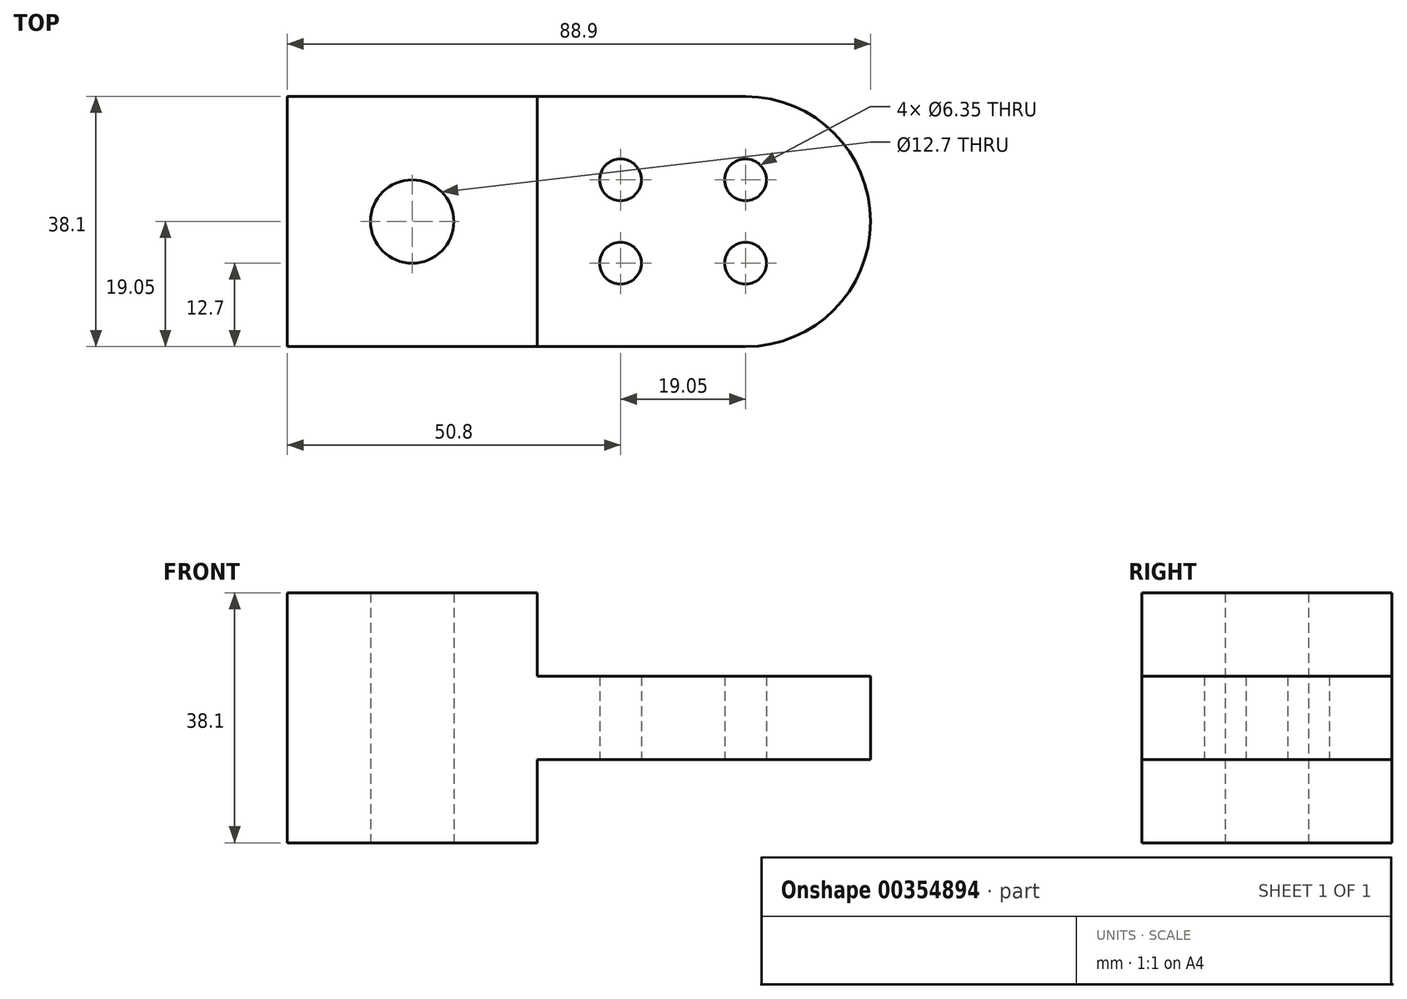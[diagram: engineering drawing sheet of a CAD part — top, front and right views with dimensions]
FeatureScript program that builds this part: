
annotation { "Feature Type Name" : "Feature", "Feature Type Description" : "" }
export const myFeature = defineFeature(function(context is Context, id is Id, definition is map)
    precondition{}
    {
        {
            var Q0;
            Q0=qCreatedBy(makeId("Top.planeOp"),FACE);
            var sketch = newSketch(context, id + "F0", { "sketchPlane" : qUnion([Q0])});
            skLineSegment(sketch, "E0", {"start": v(0, 0) * mm, "end": v(88.9, 0) * mm});
            skLineSegment(sketch, "E1", {"start": v(88.9, 0) * mm, "end": v(88.9, 38.1) * mm});
            skLineSegment(sketch, "E2", {"start": v(88.9, 38.1) * mm, "end": v(0, 38.1) * mm});
            skLineSegment(sketch, "E3", {"start": v(0, 38.1) * mm, "end": v(0, 0) * mm});
            skSolve(sketch);
        }
        {
            var Q0;
            Q0 = qSketchRegion(id + "F0", true);
            extrude(context, id + "F1", {"entities" : qUnion([Q0]), "depth" : 38.1 * mm});
        }
        {
            var Q0;
            Q0=makeQuery(id+"F1.opExtrude","CAP_FACE",FACE,{"disambiguationData":[OSD([sQuery(id+"F0.wireOp",EDGE,"E0"),sQuery(id+"F0.wireOp",EDGE,"E1"),sQuery(id+"F0.wireOp",EDGE,"E2"),sQuery(id+"F0.wireOp",EDGE,"E3")])],"isStart":false});
            var sketch = newSketch(context, id + "F2", { "sketchPlane" : qUnion([Q0])});
            skLineSegment(sketch, "E4", {"start": v(88.9, 38.1) * mm, "end": v(38.1, 38.1) * mm});
            skLineSegment(sketch, "E5", {"start": v(38.1, 38.1) * mm, "end": v(38.1, 0) * mm});
            skLineSegment(sketch, "E6", {"start": v(38.1, 0) * mm, "end": v(88.9, 0) * mm});
            skLineSegment(sketch, "E7", {"start": v(88.9, 0) * mm, "end": v(88.9, 38.1) * mm});
            skSolve(sketch);
        }
        {
            var Q0;
            Q0 = qSketchRegion(id + "F2", true);
            extrude(context, id + "F3", {"entities" : qUnion([Q0]), "operationType" : NewBodyOperationType.REMOVE, "oppositeDirection" : true, "depth" : 12.7 * mm});
        }
        {
            var Q0;
            Q0=makeQuery(id+"F1.opExtrude","CAP_FACE",FACE,{"disambiguationData":[OSD([sQuery(id+"F0.wireOp",EDGE,"E0"),sQuery(id+"F0.wireOp",EDGE,"E1"),sQuery(id+"F0.wireOp",EDGE,"E2"),sQuery(id+"F0.wireOp",EDGE,"E3")])],"isStart":true});
            var sketch = newSketch(context, id + "F4", { "sketchPlane" : qUnion([Q0])});
            skLineSegment(sketch, "E8", {"start": v(88.9, 0) * mm, "end": v(38.1, 0) * mm});
            skLineSegment(sketch, "E9", {"start": v(38.1, 0) * mm, "end": v(38.1, -38.1) * mm});
            skPoint(sketch, "E9.endSnap0", {"position": v(44.45, -38.1) * mm});
            skLineSegment(sketch, "E10", {"start": v(38.1, -38.1) * mm, "end": v(88.9, -38.1) * mm});
            skLineSegment(sketch, "E11", {"start": v(88.9, -38.1) * mm, "end": v(88.9, 0) * mm});
            skSolve(sketch);
        }
        {
            var Q0;
            Q0 = qSketchRegion(id + "F4", true);
            extrude(context, id + "F5", {"entities" : qUnion([Q0]), "operationType" : NewBodyOperationType.REMOVE, "oppositeDirection" : true, "depth" : 12.7 * mm});
        }
        {
            var Q0;
            Q0=makeQuery(id+"F1.opExtrude","CAP_FACE",FACE,{"disambiguationData":[OSD([sQuery(id+"F0.wireOp",EDGE,"E0"),sQuery(id+"F0.wireOp",EDGE,"E1"),sQuery(id+"F0.wireOp",EDGE,"E2"),sQuery(id+"F0.wireOp",EDGE,"E3")])],"isStart":true});
            var sketch = newSketch(context, id + "F6", { "sketchPlane" : qUnion([Q0])});
            skLineSegment(sketch, "E12", {"start": v(19.05, 0) * mm, "end": v(19.05, -38.1) * mm});
            skLineSegment(sketch, "E13", {"start": v(19.05, -38.1) * mm, "end": v(38.1, 0) * mm});
            skLineSegment(sketch, "E14", {"start": v(38.1, 0) * mm, "end": v(50.8, 0) * mm});
            skLineSegment(sketch, "E15", {"start": v(50.8, 0) * mm, "end": v(50.8, -38.1) * mm});
            skLineSegment(sketch, "E16", {"start": v(50.8, -38.1) * mm, "end": v(69.85, -38.1) * mm});
            skLineSegment(sketch, "E17", {"start": v(69.85, -38.1) * mm, "end": v(69.85, 0) * mm});
            skLineSegment(sketch, "E18", {"start": v(69.85, 0) * mm, "end": v(69.85, -12.7) * mm});
            skLineSegment(sketch, "E19", {"start": v(69.85, -12.7) * mm, "end": v(69.85, -38.1) * mm});
            skLineSegment(sketch, "E20", {"start": v(69.85, -25.4) * mm, "end": v(69.85, -38.1) * mm});
            skLineSegment(sketch, "E21", {"start": v(50.8, -25.4) * mm, "end": v(50.8, -38.1) * mm});
            skLineSegment(sketch, "E22", {"start": v(50.8, 0) * mm, "end": v(50.8, -12.7) * mm});
            skCircle(sketch, "E23", {"center": v(19.05, -19.05) * mm, "radius": 6.35 * mm});
            skCircle(sketch, "E24", {"center": v(50.8, -12.7) * mm, "radius": 3.18 * mm});
            skCircle(sketch, "E25", {"center": v(50.8, -25.4) * mm, "radius": 3.18 * mm});
            skCircle(sketch, "E26", {"center": v(69.85, -12.7) * mm, "radius": 3.18 * mm});
            skCircle(sketch, "E27", {"center": v(69.85, -25.4) * mm, "radius": 3.18 * mm});
            skSolve(sketch);
        }
        {
            var Q0;
            Q0 = qSketchRegion(id + "F6", true);
            extrude(context, id + "F7", {"entities" : qUnion([Q0]), "operationType" : NewBodyOperationType.REMOVE, "oppositeDirection" : true, "depth" : 177.8 * mm});
        }
        {
            var Q0;
            Q0=makeQuery(id+"F1.opExtrude","SWEPT_EDGE",EDGE,{"disambiguationData":[OSD([sQuery(id+"F0.wireOp",EDGE,"E1"),sQuery(id+"F0.wireOp",EDGE,"E2")])]});
            var Q1;
            Q1=makeQuery(id+"F1.opExtrude","SWEPT_EDGE",EDGE,{"disambiguationData":[OSD([sQuery(id+"F0.wireOp",EDGE,"E0"),sQuery(id+"F0.wireOp",EDGE,"E1")])]});
            fillet(context, id + "F8", {"entities" : qUnion([Q0, Q1]), "radius" : 19.05 * mm, "tangentPropagation" : true, "allowEdgeOverflow" : false});
        }
    });
